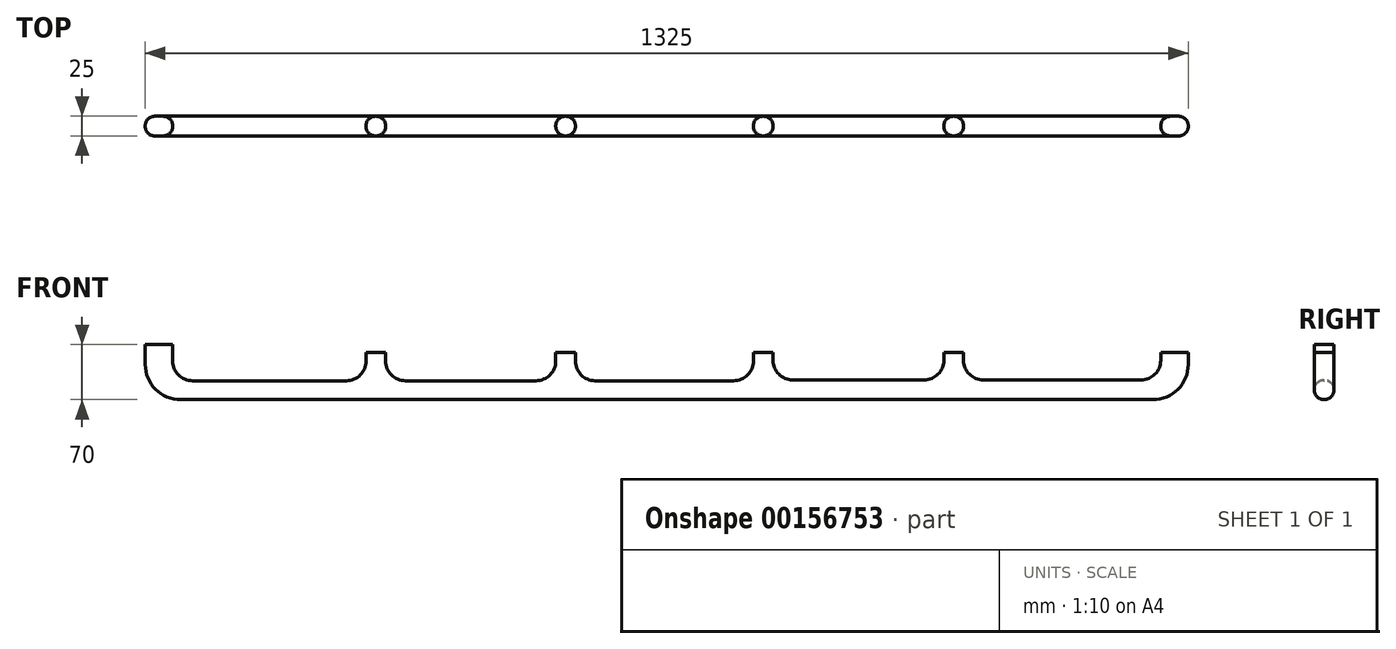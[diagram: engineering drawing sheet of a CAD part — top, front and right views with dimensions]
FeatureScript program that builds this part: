
annotation { "Feature Type Name" : "Feature", "Feature Type Description" : "" }
export const myFeature = defineFeature(function(context is Context, id is Id, definition is map)
    precondition{}
    {
        {
            var Q0;
            Q0=qCreatedBy(makeId("Front.planeOp"),FACE);
            var sketch = newSketch(context, id + "F0", { "sketchPlane" : qUnion([Q0])});
            skLineSegment(sketch, "E0.bottom", {"start": v(0, 0) * mm, "end": v(-35, 0) * mm, "construction": true});
            skLineSegment(sketch, "E0.top", {"start": v(0, 10) * mm, "end": v(-35, 10) * mm, "construction": true});
            skLineSegment(sketch, "E0.left", {"start": v(0, 0) * mm, "end": v(0, 10) * mm, "construction": true});
            skLineSegment(sketch, "E0.right", {"start": v(-35, 0) * mm, "end": v(-35, 10) * mm, "construction": true});
            skLineSegment(sketch, "E1.bottom", {"start": v(-279, 0) * mm, "end": v(-317, 0) * mm, "construction": true});
            skLineSegment(sketch, "E1.top", {"start": v(-279, 10) * mm, "end": v(-317, 10) * mm, "construction": true});
            skLineSegment(sketch, "E1.left", {"start": v(-279, 0) * mm, "end": v(-279, 10) * mm, "construction": true});
            skLineSegment(sketch, "E1.right", {"start": v(-317, 0) * mm, "end": v(-317, 10) * mm, "construction": true});
            skLineSegment(sketch, "E2.bottom", {"start": v(-517, 0) * mm, "end": v(-563, 0) * mm, "construction": true});
            skLineSegment(sketch, "E2.top", {"start": v(-517, 10) * mm, "end": v(-563, 10) * mm, "construction": true});
            skLineSegment(sketch, "E2.left", {"start": v(-517, 0) * mm, "end": v(-517, 10) * mm, "construction": true});
            skLineSegment(sketch, "E2.right", {"start": v(-563, 0) * mm, "end": v(-563, 10) * mm, "construction": true});
            skLineSegment(sketch, "E3.bottom", {"start": v(-775, 0) * mm, "end": v(-807, 0) * mm, "construction": true});
            skLineSegment(sketch, "E3.top", {"start": v(-775, 10) * mm, "end": v(-807, 10) * mm, "construction": true});
            skLineSegment(sketch, "E3.left", {"start": v(-775, 0) * mm, "end": v(-775, 10) * mm, "construction": true});
            skLineSegment(sketch, "E3.right", {"start": v(-807, 0) * mm, "end": v(-807, 10) * mm, "construction": true});
            skLineSegment(sketch, "E4.bottom", {"start": v(-1015, 0) * mm, "end": v(-1049, 0) * mm, "construction": true});
            skLineSegment(sketch, "E4.top", {"start": v(-1015, 10) * mm, "end": v(-1049, 10) * mm, "construction": true});
            skLineSegment(sketch, "E4.left", {"start": v(-1015, 0) * mm, "end": v(-1015, 10) * mm, "construction": true});
            skLineSegment(sketch, "E4.right", {"start": v(-1049, 0) * mm, "end": v(-1049, 10) * mm, "construction": true});
            skLineSegment(sketch, "E5.bottom", {"start": v(-1260, 10) * mm, "end": v(-1355, 10) * mm, "construction": true});
            skLineSegment(sketch, "E5.top", {"start": v(-1260, 21.8) * mm, "end": v(-1355, 21.8) * mm, "construction": true});
            skLineSegment(sketch, "E5.left", {"start": v(-1260, 10) * mm, "end": v(-1260, 21.8) * mm, "construction": true});
            skLineSegment(sketch, "E5.right", {"start": v(-1355, 10) * mm, "end": v(-1355, 21.8) * mm, "construction": true});
            skLineSegment(sketch, "E6", {"start": v(-1307.5, 10) * mm, "end": v(-1307.5, 21.8) * mm, "construction": true});
            skLineSegment(sketch, "E7", {"start": v(-1032, 0) * mm, "end": v(-1032, 10) * mm, "construction": true});
            skLineSegment(sketch, "E8", {"start": v(-791, 0) * mm, "end": v(-791, 25.74) * mm, "construction": true});
            skPoint(sketch, "E8.endSnap0", {"position": v(-791, 10) * mm});
            skLineSegment(sketch, "E9", {"start": v(-540, 0) * mm, "end": v(-540, 28.37) * mm, "construction": true});
            skPoint(sketch, "E9.endSnap0", {"position": v(-540, 10) * mm});
            skLineSegment(sketch, "E10", {"start": v(-298, 0) * mm, "end": v(-298, 25.62) * mm, "construction": true});
            skPoint(sketch, "E10.endSnap0", {"position": v(-298, 10) * mm});
            skLineSegment(sketch, "E11", {"start": v(-17.5, 0) * mm, "end": v(-17.5, 33.81) * mm, "construction": true});
            skLineSegment(sketch, "E12.0", {"start": v(-45, -60) * mm, "end": v(-1280, -60) * mm});
            skLineSegment(sketch, "E13", {"start": v(-1032, 0) * mm, "end": v(-1032, -60) * mm, "construction": true});
            skLineSegment(sketch, "E14", {"start": v(-791, 0) * mm, "end": v(-791, -60) * mm, "construction": true});
            skLineSegment(sketch, "E15", {"start": v(-1307.5, 10) * mm, "end": v(-1307.5, -60) * mm, "construction": true});
            skLineSegment(sketch, "E16", {"start": v(-540, 0) * mm, "end": v(-540, -60) * mm, "construction": true});
            skLineSegment(sketch, "E17", {"start": v(-298, 0) * mm, "end": v(-298, -60) * mm, "construction": true});
            skLineSegment(sketch, "E18", {"start": v(-17.5, 0) * mm, "end": v(-17.5, -60) * mm, "construction": true});
            skLineSegment(sketch, "E19.0", {"start": v(-1325, 10) * mm, "end": v(-1325, -15) * mm});
            skLineSegment(sketch, "E20.0", {"start": v(-1290, 10) * mm, "end": v(-1290, -11) * mm});
            skLineSegment(sketch, "E21.0", {"start": v(-1019.5, 0) * mm, "end": v(-1019.5, -11) * mm});
            skLineSegment(sketch, "E22.0", {"start": v(-1044.5, 0) * mm, "end": v(-1044.5, -11) * mm});
            skLineSegment(sketch, "E23.0", {"start": v(-803.5, 0) * mm, "end": v(-803.5, -11) * mm});
            skLineSegment(sketch, "E24.0", {"start": v(-778.5, 0) * mm, "end": v(-778.5, -11) * mm});
            skLineSegment(sketch, "E25.0", {"start": v(-552.5, 0) * mm, "end": v(-552.5, -11) * mm});
            skLineSegment(sketch, "E26.0", {"start": v(-527.5, 0) * mm, "end": v(-527.5, -10) * mm});
            skLineSegment(sketch, "E27.0", {"start": v(-310.5, 0) * mm, "end": v(-310.5, -10) * mm});
            skLineSegment(sketch, "E28.0", {"start": v(-285.5, 0) * mm, "end": v(-285.5, -10) * mm});
            skLineSegment(sketch, "E29.0", {"start": v(0, 0) * mm, "end": v(0, -15) * mm});
            skLineSegment(sketch, "E30.0", {"start": v(-35, 0) * mm, "end": v(-35, -10) * mm});
            skLineSegment(sketch, "E31.trimOffspring", {"start": v(-577.5, -36) * mm, "end": v(-753.5, -36) * mm});
            skLineSegment(sketch, "E32.trimOffspring", {"start": v(-335.5, -35) * mm, "end": v(-502.5, -35) * mm});
            skLineSegment(sketch, "E33.trimOffspring", {"start": v(-60, -35) * mm, "end": v(-260.5, -35) * mm});
            skLineSegment(sketch, "E34.trimOffspring", {"start": v(-828.5, -36) * mm, "end": v(-994.5, -36) * mm});
            skLineSegment(sketch, "E35.trimOffspring", {"start": v(-1069.5, -36) * mm, "end": v(-1265, -36) * mm});
            skPoint(sketch, "E36.orphan", {"position": v(-1355, -60) * mm});
            skPoint(sketch, "E37.visualSharp", {"position": v(-1290, -36) * mm});
            skArc(sketch, "E37.filletArc", {"start": v(-1290, -11) * mm, "mid": v(-1282.68, -28.68) * mm, "end": v(-1265, -36) * mm});
            skPoint(sketch, "E38.visualSharp", {"position": v(-1044.5, -36) * mm});
            skArc(sketch, "E38.filletArc", {"start": v(-1069.5, -36) * mm, "mid": v(-1051.82, -28.68) * mm, "end": v(-1044.5, -11) * mm});
            skPoint(sketch, "E39.visualSharp", {"position": v(-1019.5, -36) * mm});
            skArc(sketch, "E39.filletArc", {"start": v(-1019.5, -11) * mm, "mid": v(-1012.18, -28.68) * mm, "end": v(-994.5, -36) * mm});
            skPoint(sketch, "E40.visualSharp", {"position": v(-803.5, -36) * mm});
            skArc(sketch, "E40.filletArc", {"start": v(-828.5, -36) * mm, "mid": v(-810.82, -28.68) * mm, "end": v(-803.5, -11) * mm});
            skPoint(sketch, "E41.visualSharp", {"position": v(-778.5, -36) * mm});
            skArc(sketch, "E41.filletArc", {"start": v(-778.5, -11) * mm, "mid": v(-771.18, -28.68) * mm, "end": v(-753.5, -36) * mm});
            skPoint(sketch, "E42.visualSharp", {"position": v(-527.5, -35) * mm});
            skArc(sketch, "E42.filletArc", {"start": v(-527.5, -10) * mm, "mid": v(-520.18, -27.68) * mm, "end": v(-502.5, -35) * mm});
            skPoint(sketch, "E43.visualSharp", {"position": v(-552.5, -36) * mm});
            skArc(sketch, "E43.filletArc", {"start": v(-577.5, -36) * mm, "mid": v(-559.82, -28.68) * mm, "end": v(-552.5, -11) * mm});
            skPoint(sketch, "E44.visualSharp", {"position": v(-310.5, -35) * mm});
            skArc(sketch, "E44.filletArc", {"start": v(-335.5, -35) * mm, "mid": v(-317.82, -27.68) * mm, "end": v(-310.5, -10) * mm});
            skPoint(sketch, "E45.visualSharp", {"position": v(-285.5, -35) * mm});
            skArc(sketch, "E45.filletArc", {"start": v(-285.5, -10) * mm, "mid": v(-278.18, -27.68) * mm, "end": v(-260.5, -35) * mm});
            skPoint(sketch, "E46.visualSharp", {"position": v(-35, -35) * mm});
            skArc(sketch, "E46.filletArc", {"start": v(-60, -35) * mm, "mid": v(-42.32, -27.68) * mm, "end": v(-35, -10) * mm});
            skPoint(sketch, "E47.visualSharp", {"position": v(0, -60) * mm});
            skArc(sketch, "E47.filletArc", {"start": v(-45, -60) * mm, "mid": v(-13.18, -46.82) * mm, "end": v(0, -15) * mm});
            skPoint(sketch, "E48.visualSharp", {"position": v(-1325, -60) * mm});
            skArc(sketch, "E48.filletArc", {"start": v(-1325, -15) * mm, "mid": v(-1311.82, -46.82) * mm, "end": v(-1280, -60) * mm});
            skLineSegment(sketch, "E49", {"start": v(-1290, 10) * mm, "end": v(-1325, 10) * mm});
            skLineSegment(sketch, "E50", {"start": v(-1019.5, 0) * mm, "end": v(-1044.5, 0) * mm});
            skLineSegment(sketch, "E51", {"start": v(-778.5, 0) * mm, "end": v(-803.5, 0) * mm});
            skLineSegment(sketch, "E52", {"start": v(-527.5, 0) * mm, "end": v(-552.5, 0) * mm});
            skLineSegment(sketch, "E53", {"start": v(-285.5, 0) * mm, "end": v(-310.5, 0) * mm});
            skLineSegment(sketch, "E54", {"start": v(0, 0) * mm, "end": v(-35, 0) * mm});
            skSolve(sketch);
        }
        {
            var Q0;
            Q0=makeQuery(id+"F0.imprint","IMPRINT",FACE,{"disambiguationData":[TD([[makeQuery(id+"F0.imprint","IMPRINT",EDGE,{"derivedFrom":sQuery(id+"F0.wireOp",EDGE,"E12.0")}),-1.0]])]});
            extrude(context, id + "F1", {"entities" : qUnion([Q0]), "depth" : 25 * mm});
        }
        {
            var Q0;
            Q0=makeQuery(id+"F1.opExtrude","CAP_EDGE",EDGE,{"disambiguationData":[OSD([sQuery(id+"F0.wireOp",EDGE,"E46.filletArc")])],"isStart":true});
            var Q1;
            Q1=makeQuery(id+"F1.opExtrude","CAP_EDGE",EDGE,{"disambiguationData":[OSD([sQuery(id+"F0.wireOp",EDGE,"E12.0")])],"isStart":true});
            var Q2;
            Q2=makeQuery(id+"F1.opExtrude","CAP_EDGE",EDGE,{"disambiguationData":[OSD([sQuery(id+"F0.wireOp",EDGE,"E44.filletArc")])],"isStart":true});
            var Q3;
            Q3=makeQuery(id+"F1.opExtrude","CAP_EDGE",EDGE,{"disambiguationData":[OSD([sQuery(id+"F0.wireOp",EDGE,"E43.filletArc")])],"isStart":true});
            var Q4;
            Q4=makeQuery(id+"F1.opExtrude","CAP_EDGE",EDGE,{"disambiguationData":[OSD([sQuery(id+"F0.wireOp",EDGE,"E40.filletArc")])],"isStart":true});
            var Q5;
            Q5=makeQuery(id+"F1.opExtrude","CAP_EDGE",EDGE,{"disambiguationData":[OSD([sQuery(id+"F0.wireOp",EDGE,"E38.filletArc")])],"isStart":true});
            var Q6;
            Q6=makeQuery(id+"F1.opExtrude","CAP_EDGE",EDGE,{"disambiguationData":[OSD([sQuery(id+"F0.wireOp",EDGE,"E48.filletArc")])],"isStart":false});
            var Q7;
            Q7=makeQuery(id+"F1.opExtrude","CAP_EDGE",EDGE,{"disambiguationData":[OSD([sQuery(id+"F0.wireOp",EDGE,"E37.filletArc")])],"isStart":false});
            var Q8;
            Q8=makeQuery(id+"F1.opExtrude","CAP_EDGE",EDGE,{"disambiguationData":[OSD([sQuery(id+"F0.wireOp",EDGE,"E34.trimOffspring")])],"isStart":false});
            var Q9;
            Q9=makeQuery(id+"F1.opExtrude","CAP_EDGE",EDGE,{"disambiguationData":[OSD([sQuery(id+"F0.wireOp",EDGE,"E31.trimOffspring")])],"isStart":false});
            var Q10;
            Q10=makeQuery(id+"F1.opExtrude","CAP_EDGE",EDGE,{"disambiguationData":[OSD([sQuery(id+"F0.wireOp",EDGE,"E32.trimOffspring")])],"isStart":false});
            var Q11;
            Q11=makeQuery(id+"F1.opExtrude","CAP_EDGE",EDGE,{"disambiguationData":[OSD([sQuery(id+"F0.wireOp",EDGE,"E33.trimOffspring")])],"isStart":false});
            fillet(context, id + "F2", {"entities" : qUnion([Q0, Q1, Q2, Q3, Q4, Q5, Q6, Q7, Q8, Q9, Q10, Q11]), "radius" : 12 * mm, "tangentPropagation" : true, "allowEdgeOverflow" : false});
        }
    });
